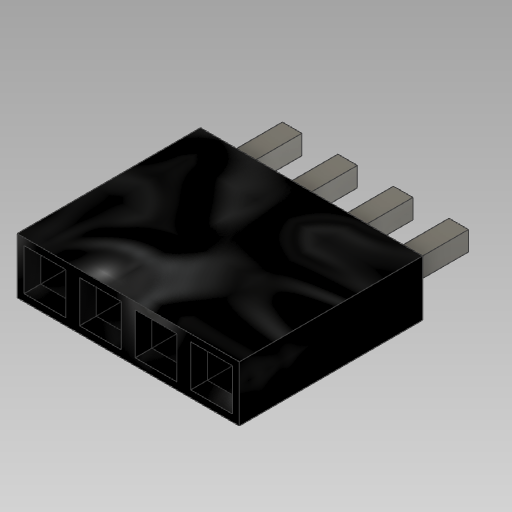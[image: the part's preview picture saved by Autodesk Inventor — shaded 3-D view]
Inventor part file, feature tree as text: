
AUTODESK INVENTOR PART (.ipt)
format: ipt  version: 2020 (Build 240168000, 168)  size: 221,696 bytes
history: native  units: in
note: dims shown in document units (in); Inventor stores cm internally (conversion verified against a paired STEP export)
features: extrude x3, sketch x3, chamfer x2, other x2, pattern_linear x1
ambient origin geometry x8: Origin, YZ Plane, XZ Plane, XY Plane, X Axis, Y Axis, Z Axis, Center Point
bodies: Solid1 (feature_tree)
feature tree (11):
  extrude  "Extrusion1"  Depth=0.1in
  extrude  "Extrusion2"  Depth=0.045in
  chamfer  "Chamfer1"  Distance=0.25in
  extrude  "Extrusion3"  Depth=0.035in
  chamfer  "Chamfer2"  Distance=0.13in
  pattern_linear  "Rectangular Pattern1"  Spacing1=0.015in  [1 undecoded]
  other  "Work Axis1"
  sketch  "Sketch1"  dims[d0=0.1in d1=0.1in]
  sketch  "Sketch2"  dims[d2=0.33in d3=0.0in d4=0.045in d5=0.25in d6=0.0in]
  sketch  "Sketch3"  dims[d7=0.015in d8=0.125in d9=45.0deg d10=0.035in d11=0.13in d12=0.0in d13=0.015in d14=0.125in d15=45.0deg d16=1.5748in d18=0.1in]
  other  "Work Point1"
note: 1 required parameter value undecoded (feature->parameter linkage not recoverable at this tier; creation-order binding heuristic only, values carry confidence <= 0.55)
